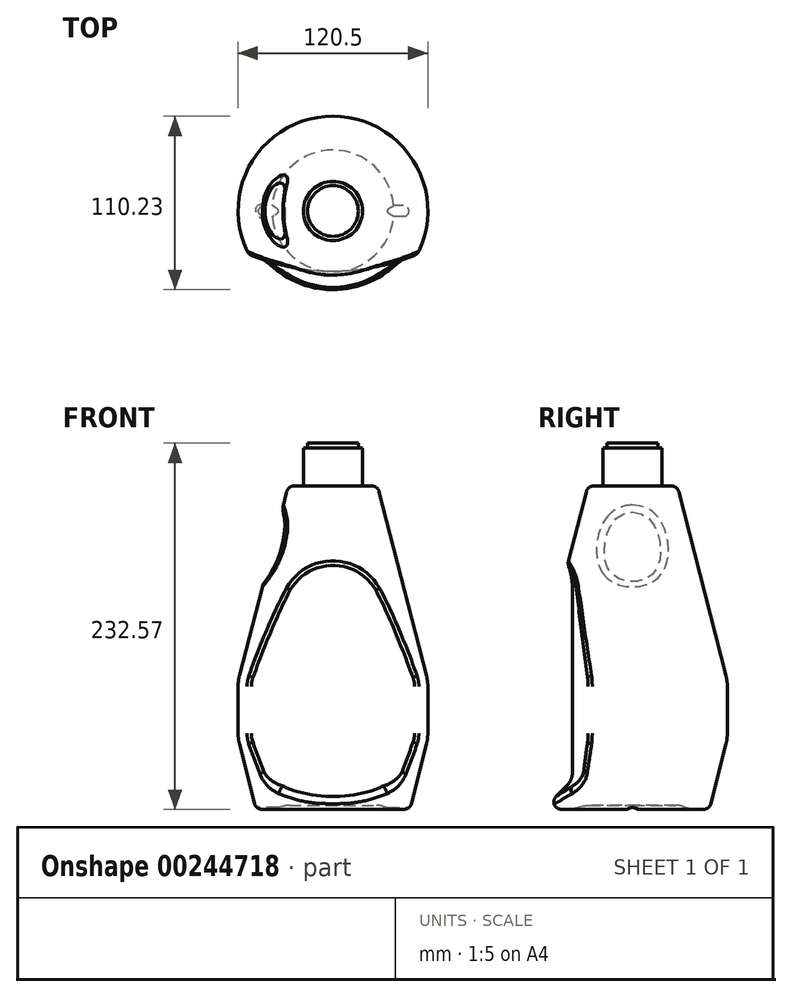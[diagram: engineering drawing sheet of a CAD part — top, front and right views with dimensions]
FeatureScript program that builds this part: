
annotation { "Feature Type Name" : "Feature", "Feature Type Description" : "" }
export const myFeature = defineFeature(function(context is Context, id is Id, definition is map)
    precondition{}
    {
        {
            var Q0;
            Q0=qCreatedBy(makeId("Front.planeOp"),FACE);
            var sketch = newSketch(context, id + "F0", { "sketchPlane" : qUnion([Q0])});
            skLineSegment(sketch, "E0", {"start": v(-60.25, -8.59) * mm, "end": v(-60.25, -45.26) * mm});
            skLineSegment(sketch, "E1", {"start": v(-60.25, -45.26) * mm, "end": v(-49.01, -90.15) * mm});
            skLineSegment(sketch, "E2", {"start": v(-49.01, -90.15) * mm, "end": v(0, -90.15) * mm});
            skLineSegment(sketch, "E3", {"start": v(0, -90.15) * mm, "end": v(0, 115.38) * mm});
            skLineSegment(sketch, "E4", {"start": v(0, 115.38) * mm, "end": v(-28.4, 115.38) * mm});
            skLineSegment(sketch, "E5", {"start": v(-28.4, 115.38) * mm, "end": v(-60.25, -8.59) * mm});
            skSolve(sketch);
        }
        {
            var Q0;
            Q0 = qSketchRegion(id + "F0", true);
            var Q1;
            Q1=sQuery(id+"F0.wireOp",EDGE,"E3");
            revolve(context, id + "F1", {"entities" : qUnion([Q0]), "axis" : qUnion([Q1]), "revolveType" : RevolveType.FULL});
        }
        {
            var Q0;
            Q0=qCreatedBy(makeId("Right.planeOp"),FACE);
            var sketch = newSketch(context, id + "F2", { "sketchPlane" : qUnion([Q0])});
            skLineSegment(sketch, "E6", {"start": v(-38.1, 70.13) * mm, "end": v(-38.1, -71.65) * mm});
            skLineSegment(sketch, "E7", {"start": v(-38.1, -71.65) * mm, "end": v(-72.47, -106.02) * mm});
            skLineSegment(sketch, "E8", {"start": v(-38.1, 70.13) * mm, "end": v(-72.47, 104.5) * mm});
            skLineSegment(sketch, "E9", {"start": v(-72.47, 104.5) * mm, "end": v(-72.47, -106.02) * mm});
            skLineSegment(sketch, "E10", {"start": v(101.6, 94.9) * mm, "end": v(101.6, -87.73) * mm});
            skSolve(sketch);
        }
        {
            var Q0;
            Q0 = qSketchRegion(id + "F2", true);
            var Q1;
            Q1=sQuery(id+"F2.wireOp",EDGE,"E10");
            revolve(context, id + "F3", {"operationType" : NewBodyOperationType.REMOVE, "entities" : qUnion([Q0]), "axis" : qUnion([Q1]), "revolveType" : RevolveType.FULL, "oppositeDirection" : true});
        }
        {
            var Q0;
            Q0=makeQuery(id+"F3uHGruwqN1f3uc_1.1.F3.boolean.opBoolean","COPY",EDGE,{"derivedFrom":makeQuery(id+"F3uHGruwqN1f3uc_1.1.F3.opRevolve","SWEPT_EDGE",EDGE,{"disambiguationData":[OSD([sQuery(id+"F2.wireOp",EDGE,"E6"),sQuery(id+"F2.wireOp",EDGE,"E8")])]})});
            var Q1;
            Q1=makeQuery(id+"F3.boolean.opBoolean","COPY",EDGE,{"derivedFrom":makeQuery(id+"F3.opRevolve","SWEPT_EDGE",EDGE,{"disambiguationData":[OSD([sQuery(id+"F2.wireOp",EDGE,"E6"),sQuery(id+"F2.wireOp",EDGE,"E8")])]})});
            fillet(context, id + "F4", {"entities" : qUnion([Q0, Q1]), "radius" : 50.8 * mm, "tangentPropagation" : true, "allowEdgeOverflow" : false});
        }
        {
            var Q0;
            Q0=makeQuery(id+"F3uHGruwqN1f3uc_1.1.F3.boolean.opBoolean","COPY",EDGE,{"derivedFrom":makeQuery(id+"F3uHGruwqN1f3uc_1.1.F3.opRevolve","SWEPT_EDGE",EDGE,{"disambiguationData":[OSD([sQuery(id+"F2.wireOp",EDGE,"E6"),sQuery(id+"F2.wireOp",EDGE,"E7")])]})});
            var Q1;
            Q1=makeQuery(id+"F3.boolean.opBoolean","COPY",EDGE,{"derivedFrom":makeQuery(id+"F3.opRevolve","SWEPT_EDGE",EDGE,{"disambiguationData":[OSD([sQuery(id+"F2.wireOp",EDGE,"E6"),sQuery(id+"F2.wireOp",EDGE,"E7")])]})});
            fillet(context, id + "F5", {"entities" : qUnion([Q0, Q1]), "radius" : 12.7 * mm, "tangentPropagation" : true, "allowEdgeOverflow" : false});
        }
        {
            var Q0;
            Q0=qCreatedBy(makeId("Front.planeOp"),FACE);
            var sketch = newSketch(context, id + "F6", { "sketchPlane" : qUnion([Q0])});
            skEllipse(sketch, "E11", {"center": v(-50.43, 76.59) * mm, "majorRadius": 33.74 * mm, "minorRadius": 17.1 * mm, "majorAxis": v(-0.35, -0.94)});
            skSolve(sketch);
        }
        {
            var Q0;
            Q0 = qSketchRegion(id + "F6", true);
            extrude(context, id + "F7", {"entities" : qUnion([Q0]), "operationType" : NewBodyOperationType.REMOVE, "endBound" : BoundingType.THROUGH_ALL, "depth" : 25.4 * mm, "hasSecondDirection" : true, "secondDirectionBound" : SecondDirectionBoundingType.THROUGH_ALL, "secondDirectionOppositeDirection" : true, "secondDirectionDepth" : 25.4 * mm});
        }
        {
            var Q0;
            Q0=makeQuery(id+"FcOrjPNq3cfCj5B_1.1.F7.boolean.opBoolean","INTERSECT",EDGE,{"derivedFrom":[makeQuery(id+"F1.opRevolve","SWEPT_FACE",FACE,{"disambiguationData":[OSD([sQuery(id+"F0.wireOp",EDGE,"E5")])]}),makeQuery(id+"FcOrjPNq3cfCj5B_1.1.F7.opExtrude","SWEPT_FACE",FACE,{"disambiguationData":[OSD([sQuery(id+"F6.wireOp",EDGE,"E11")])]})]});
            var Q1;
            Q1=makeQuery(id+"F7.boolean.opBoolean","INTERSECT",EDGE,{"derivedFrom":[makeQuery(id+"F1.opRevolve","SWEPT_FACE",FACE,{"disambiguationData":[OSD([sQuery(id+"F0.wireOp",EDGE,"E5")])]}),makeQuery(id+"F7.opExtrude","SWEPT_FACE",FACE,{"disambiguationData":[OSD([sQuery(id+"F6.wireOp",EDGE,"E11")])]})]});
            fillet(context, id + "F8", {"entities" : qUnion([Q0, Q1]), "radius" : 8.97 * mm, "tangentPropagation" : true, "allowEdgeOverflow" : false});
        }
        {
            var Q0;
            Q0=makeQuery(id+"F1.opRevolve","SWEPT_EDGE",EDGE,{"disambiguationData":[OSD([sQuery(id+"F0.wireOp",EDGE,"E4"),sQuery(id+"F0.wireOp",EDGE,"E5")])]});
            fillet(context, id + "F9", {"entities" : qUnion([Q0]), "radius" : 5.08 * mm, "tangentPropagation" : true, "allowEdgeOverflow" : false});
        }
        {
            var Q0;
            Q0=makeQuery(id+"F3uHGruwqN1f3uc_1.1.F3.boolean.opBoolean","SPLIT",EDGE,{"disambiguationData":[OD(0.0)],"derivedFrom":makeQuery(id+"F1.opRevolve","SWEPT_EDGE",EDGE,{"disambiguationData":[OSD([sQuery(id+"F0.wireOp",EDGE,"E0"),sQuery(id+"F0.wireOp",EDGE,"E5")])]})});
            var Q1;
            Q1=makeQuery(id+"F3uHGruwqN1f3uc_1.1.F3.boolean.opBoolean","SPLIT",EDGE,{"disambiguationData":[OD(0.0)],"derivedFrom":makeQuery(id+"F1.opRevolve","SWEPT_EDGE",EDGE,{"disambiguationData":[OSD([sQuery(id+"F0.wireOp",EDGE,"E0"),sQuery(id+"F0.wireOp",EDGE,"E1")])]})});
            var Q2;
            Q2=makeQuery(id+"F3uHGruwqN1f3uc_1.1.F3.boolean.opBoolean","SPLIT",EDGE,{"disambiguationData":[OD(1.0)],"derivedFrom":makeQuery(id+"F1.opRevolve","SWEPT_EDGE",EDGE,{"disambiguationData":[OSD([sQuery(id+"F0.wireOp",EDGE,"E0"),sQuery(id+"F0.wireOp",EDGE,"E5")])]})});
            var Q3;
            Q3=makeQuery(id+"F3uHGruwqN1f3uc_1.1.F3.boolean.opBoolean","SPLIT",EDGE,{"disambiguationData":[OD(1.0)],"derivedFrom":makeQuery(id+"F1.opRevolve","SWEPT_EDGE",EDGE,{"disambiguationData":[OSD([sQuery(id+"F0.wireOp",EDGE,"E0"),sQuery(id+"F0.wireOp",EDGE,"E1")])]})});
            fillet(context, id + "F10", {"entities" : qUnion([Q0, Q1, Q2, Q3]), "radius" : 27.94 * mm, "tangentPropagation" : true, "allowEdgeOverflow" : false});
        }
        {
            var Q0;
            Q0=makeQuery(id+"F3.boolean.opBoolean","INTERSECT",EDGE,{"disambiguationData":[OD(0.0)],"derivedFrom":[makeQuery(id+"F1.opRevolve","SWEPT_FACE",FACE,{"disambiguationData":[OSD([sQuery(id+"F0.wireOp",EDGE,"E5")])]}),makeQuery(id+"F3.opRevolve","SWEPT_FACE",FACE,{"disambiguationData":[OSD([sQuery(id+"F2.wireOp",EDGE,"E6")])]})]});
            var Q1;
            Q1=makeQuery(id+"F3uHGruwqN1f3uc_1.1.F3.boolean.opBoolean","INTERSECT",EDGE,{"disambiguationData":[OD(0.0)],"derivedFrom":[makeQuery(id+"F1.opRevolve","SWEPT_FACE",FACE,{"disambiguationData":[OSD([sQuery(id+"F0.wireOp",EDGE,"E5")])]}),makeQuery(id+"F3uHGruwqN1f3uc_1.1.F3.opRevolve","SWEPT_FACE",FACE,{"disambiguationData":[OSD([sQuery(id+"F2.wireOp",EDGE,"E6")])]})]});
            fillet(context, id + "F11", {"entities" : qUnion([Q0, Q1]), "radius" : 5.08 * mm, "tangentPropagation" : true, "allowEdgeOverflow" : false});
        }
        {
            var Q0;
            Q0=makeQuery(id+"F1.opRevolve","SWEPT_EDGE",EDGE,{"disambiguationData":[OSD([sQuery(id+"F0.wireOp",EDGE,"E1"),sQuery(id+"F0.wireOp",EDGE,"E2")])]});
            fillet(context, id + "F12", {"entities" : qUnion([Q0]), "radius" : 5.08 * mm, "tangentPropagation" : true, "allowEdgeOverflow" : false});
        }
        {
            var Q0;
            Q0=makeQuery(id+"F1.opRevolve","SWEPT_FACE",FACE,{"disambiguationData":[OSD([sQuery(id+"F0.wireOp",EDGE,"E2")])]});
            var sketch = newSketch(context, id + "F13", { "sketchPlane" : qUnion([Q0])});
            skCircle(sketch, "E12.0", {"center": v(0, 0) * mm, "radius": 38.7 * mm});
            skSolve(sketch);
        }
        {
            var Q0;
            Q0=makeQuery(id+"F13.imprint","IMPRINT",FACE,{"disambiguationData":[TD([[makeQuery(id+"F13.imprint","IMPRINT",EDGE,{"derivedFrom":sQuery(id+"F13.wireOp",EDGE,"E12.0")}),1.0]])]});
            extrude(context, id + "F14", {"entities" : qUnion([Q0]), "operationType" : NewBodyOperationType.REMOVE, "oppositeDirection" : true, "depth" : 2.54 * mm, "hasDraft" : true, "draftAngle" : 74 * degree, "draftPullDirection" : true});
        }
        {
            var Q0;
            Q0=makeQuery(id+"F14.boolean.opBoolean","COPY",EDGE,{"derivedFrom":makeQuery(id+"F14.opExtrude","CAP_EDGE",EDGE,{"disambiguationData":[OSD([sQuery(id+"F13.wireOp",EDGE,"E12.0")])],"isStart":false})});
            var Q1;
            Q1=makeQuery(id+"F14.boolean.opBoolean","COPY",EDGE,{"derivedFrom":makeQuery(id+"F14.opExtrude","CAP_EDGE",EDGE,{"disambiguationData":[OSD([sQuery(id+"F13.wireOp",EDGE,"E12.0")])],"isStart":true})});
            fillet(context, id + "F15", {"entities" : qUnion([Q0, Q1]), "radius" : 15.24 * mm, "tangentPropagation" : true, "allowEdgeOverflow" : false});
        }
        {
            var Q0;
            Q0=qCreatedBy(makeId("Right.planeOp"),FACE);
            var sketch = newSketch(context, id + "F16", { "sketchPlane" : qUnion([Q0])});
            skEllipse(sketch, "E13", {"center": v(0, -110.14) * mm, "majorRadius": 21.13 * mm, "minorRadius": 10.4 * mm, "majorAxis": v(0, 1)});
            skSolve(sketch);
        }
        {
            var Q0;
            Q0 = qSketchRegion(id + "F16", true);
            extrude(context, id + "F17", {"entities" : qUnion([Q0]), "operationType" : NewBodyOperationType.REMOVE, "endBound" : BoundingType.THROUGH_ALL, "depth" : 25.4 * mm, "hasSecondDirection" : true, "secondDirectionBound" : SecondDirectionBoundingType.THROUGH_ALL, "secondDirectionOppositeDirection" : true, "secondDirectionDepth" : 25.4 * mm});
        }
        {
            var Q0;
            {var subQ0=sQuery(id+"F13.wireOp",EDGE,"E12.0");Q0=makeQuery(id+"F17.boolean.opBoolean","INTERSECT",EDGE,{"disambiguationData":[OD(3.0)],"derivedFrom":[makeQuery(id+"F15.opFillet","BLEND_FACE",FACE,{"disambiguationData":[OSD([subQ0]),TDD([makeQuery(id+"F14.boolean.opBoolean","COPY",EDGE,{"derivedFrom":makeQuery(id+"F14.opExtrude","CAP_EDGE",EDGE,{"disambiguationData":[OSD([subQ0])],"isStart":true})})])]}),makeQuery(id+"F17.opExtrude","SWEPT_FACE",FACE,{"disambiguationData":[OSD([sQuery(id+"F16.wireOp",EDGE,"E13")])]})]});}
            var Q1;
            Q1=makeQuery(id+"F17.boolean.opBoolean","INTERSECT",EDGE,{"disambiguationData":[OD(1.0)],"derivedFrom":[makeQuery(id+"F1.opRevolve","SWEPT_FACE",FACE,{"disambiguationData":[OSD([sQuery(id+"F0.wireOp",EDGE,"E2")])]}),makeQuery(id+"F17.opExtrude","SWEPT_FACE",FACE,{"disambiguationData":[OSD([sQuery(id+"F16.wireOp",EDGE,"E13")])]})]});
            fillet(context, id + "F18", {"entities" : qUnion([Q0, Q1]), "radius" : 2.54 * mm, "tangentPropagation" : true, "allowEdgeOverflow" : false});
        }
        {
            var Q0;
            Q0=qCreatedBy(makeId("Front.planeOp"),FACE);
            var sketch = newSketch(context, id + "F19", { "sketchPlane" : qUnion([Q0])});
            skLineSegment(sketch, "E14", {"start": v(18.8, 111.18) * mm, "end": v(18.8, 139.28) * mm});
            skLineSegment(sketch, "E15", {"start": v(18.8, 139.28) * mm, "end": v(16.08, 139.28) * mm});
            skLineSegment(sketch, "E16", {"start": v(16.08, 139.28) * mm, "end": v(16.08, 142.42) * mm});
            skLineSegment(sketch, "E17", {"start": v(16.08, 142.42) * mm, "end": v(0, 142.42) * mm});
            skLineSegment(sketch, "E18", {"start": v(0, 142.42) * mm, "end": v(0, 111.18) * mm});
            skLineSegment(sketch, "E19", {"start": v(0, 111.18) * mm, "end": v(18.8, 111.18) * mm});
            skSolve(sketch);
        }
        {
            var Q0;
            Q0 = qSketchRegion(id + "F19", true);
            var Q1;
            Q1=sQuery(id+"F19.wireOp",EDGE,"E18");
            revolve(context, id + "F20", {"operationType" : NewBodyOperationType.ADD, "entities" : qUnion([Q0]), "axis" : qUnion([Q1]), "revolveType" : RevolveType.FULL});
        }
        {
            var Q0;
            Q0=makeQuery(id+"F20.boolean.opBoolean","INTERSECT",EDGE,{"derivedFrom":[makeQuery(id+"F1.opRevolve","SWEPT_FACE",FACE,{"disambiguationData":[OSD([sQuery(id+"F0.wireOp",EDGE,"E4")])]}),makeQuery(id+"F20.opRevolve","SWEPT_FACE",FACE,{"disambiguationData":[OSD([sQuery(id+"F19.wireOp",EDGE,"E14")])]})]});
            fillet(context, id + "F21", {"entities" : qUnion([Q0]), "radius" : 1.27 * mm, "tangentPropagation" : true, "allowEdgeOverflow" : false});
        }
    });
